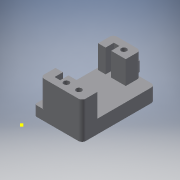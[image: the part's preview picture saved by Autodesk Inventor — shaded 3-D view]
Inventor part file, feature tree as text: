
AUTODESK INVENTOR PART (.ipt)
format: ipt  version: 2018 (Build 220112000, 112)  size: 240,128 bytes
history: native  units: mm
features: reference x12, sketch x7, other x7, extrude x6, plane x4, fillet x3, projected_geometry x2
ambient origin geometry x8: Origin, YZ Plane, XZ Plane, XY Plane, X Axis, Y Axis, Z Axis, Center Point
bodies: Solid1 (feature_tree)
feature tree (41):
  sketch  "Sketch1"  dims[d0=1.0mm d1=40.0mm]
  plane  "Work Plane1"
  extrude  "Extrusion1"  Depth=40.0mm
  sketch  "Sketch2"  dims[d2=0.0mm d3=30.0mm]
  plane  "Work Plane2"
  extrude  "Extrusion2"  Depth=30.0mm
  extrude  "Extrusion3"  TaperAngle=0.0deg  [1 undecoded]
  fillet  "Fillet1"  Radius=10.0mm
  sketch  "Sketch4"  dims[d9=4.0mm d10=4.0mm]
  sketch  "Sketch5"  dims[d11=3.0mm d12=5.0mm d13=0.0mm d14=2.0mm]
  plane  "Work Plane3"
  extrude  "Extrusion4"  Depth=4.0mm
  extrude  "Extrusion5"  Depth=5.0mm TaperAngle=0.0deg
  fillet  "Fillet2"  Radius=2.0mm
  sketch  "Sketch7"  dims[d25=3.0mm d26=3.0mm d27=7.0mm d28=0.0mm d29=2.0mm d30=3.1mm d32=10.0mm d33=0.0mm d36=1.0mm d39=50.0mm d40=5.0mm]
  plane  "Work Plane4"
  extrude  "Extrusion6"  Depth=5.0mm TaperAngle=0.0deg
  fillet  "Fillet3"  Radius=3.0mm
  reference  "Reference1"
  reference  "Reference2"
  reference  "Reference3"
  projected_geometry  "Projected Loop1"
  sketch  "Sketch3"  dims[d4=0.0mm d5=0.0mm d6=0.0mm d7=10.0mm d8=0.0mm]
  reference  "Reference4"
  reference  "Reference5"
  reference  "Reference6"
  reference  "Reference7"
  reference  "Reference8"
  reference  "Reference9"
  sketch  "Sketch6"  dims[d21=2.0mm d22=5.0mm d23=0.0mm d24=3.0mm]
  reference  "Reference10"
  reference  "Reference11"
  reference  "Reference12"
  projected_geometry  "Projected Loop2"
  other  "<userpath>\OneDrive\Documents\Inventor\TSA\2018\Animatronics\Tortoise\Turtle3.iam"
  other  "Turtle3.iam"
  other  "ButtonMountLegs:2"
  other  "servo (2):8"
  other  "SyringeServoBaseClamp:1"
  other  "SyringeServoBaseClamp:2"
  other  "HeadOpenRack:1"
note: 1 required parameter value undecoded (feature->parameter linkage not recoverable at this tier; creation-order binding heuristic only, values carry confidence <= 0.55)
